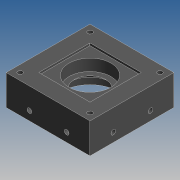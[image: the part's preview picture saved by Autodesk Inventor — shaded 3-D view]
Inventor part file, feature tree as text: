
AUTODESK INVENTOR PART (.ipt)
format: ipt  version: 2015 SP1 (Build 190203100, 203)  size: 265,728 bytes
history: native  units: mm
features: sketch x6, hole x4, extrude x2, chamfer x1, plane x1, mirror x1, pattern_circular x1
ambient origin geometry x8: Origin, YZ Plane, XZ Plane, XY Plane, X Axis, Y Axis, Z Axis, Center Point
bodies: Solid1 (feature_tree)
feature tree (16):
  extrude  "Extrusion1"  Depth=18.0mm
  extrude  "Extrusion2"  Depth=11.0mm
  hole  "M3/6/10"  [1 undecoded]
  hole  "Hole2"  [1 undecoded]
  chamfer  "Chamfer1"  Distance=2.0mm Angle=45.0deg
  hole  "Hole3"  [1 undecoded]
  hole  "M3/5/7"  [1 undecoded]
  plane  "Work Plane1"
  mirror  "Mirror1"
  pattern_circular  "Circular Pattern1"  [2 undecoded]
  sketch  "Sketch1"  dims[d0=18.0mm d1=18.0mm]
  sketch  "Sketch2"  dims[d2=13.0mm d3=0.0mm d4=11.0mm]
  sketch  "Sketch3"  dims[d5=11.0mm d6=1.0mm d7=0.0mm]
  sketch  "Sketch4"  dims[d8=15.0mm d9=15.0mm]
  sketch  "Sketch5"  dims[d10=2.0mm d11=6.0mm d12=4.0mm d13=2.0mm d14=90.0deg d15=2.0mm d16=0.0mm]
  sketch  "Sketch7"  dims[d17=12.5mm d18=6.0mm d19=24.0mm d20=5.5mm d21=90.0deg d22=10.0mm d23=20.594885mm d24=2.0mm d25=2.0mm d26=45.0deg d27=18.0mm d28=6.0mm d29=28.0mm d30=5.5mm d31=90.0deg d32=5.0mm d33=0.0mm d34=40.0mm d35=360.0deg d40=3.8mm d41=8.0mm d42=2.0mm d43=5.0mm d44=28.0mm d45=5.5mm d46=90.0deg d47=2.0mm d48=0.0mm]
note: 6 required parameter values undecoded (feature->parameter linkage not recoverable at this tier; creation-order binding heuristic only, values carry confidence <= 0.55)
